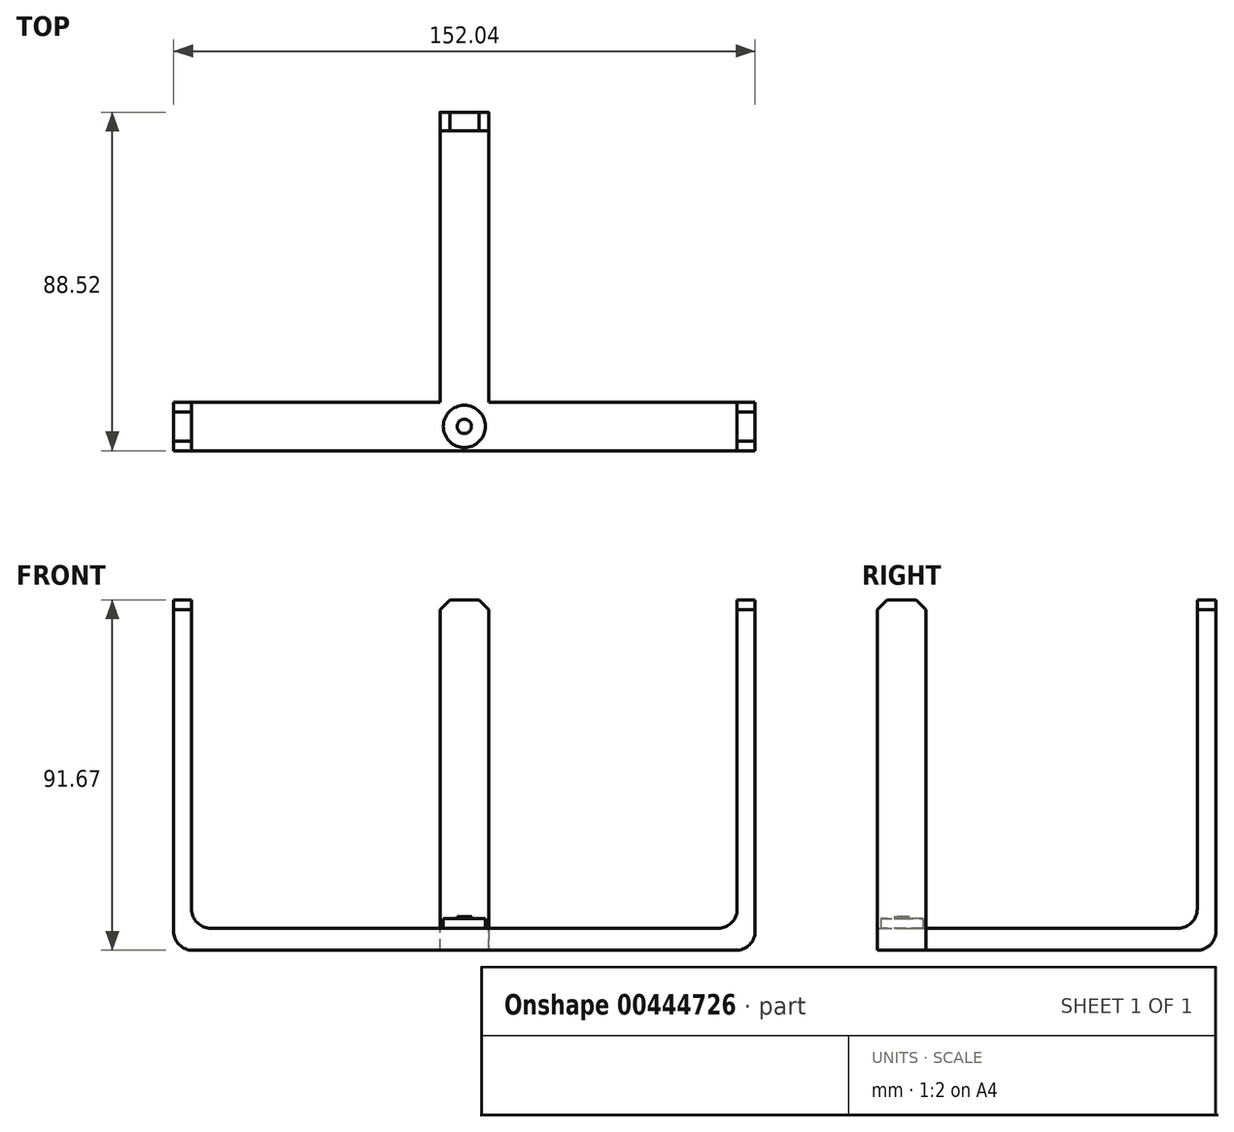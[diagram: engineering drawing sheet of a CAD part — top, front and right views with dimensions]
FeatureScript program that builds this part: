
annotation { "Feature Type Name" : "Feature", "Feature Type Description" : "" }
export const myFeature = defineFeature(function(context is Context, id is Id, definition is map)
    precondition{}
    {
        {
            var Q0;
            Q0=qCreatedBy(makeId("Front.planeOp"),FACE);
            var sketch = newSketch(context, id + "F0", { "sketchPlane" : qUnion([Q0])});
            skLineSegment(sketch, "E0", {"start": v(0, 97.69) * mm, "end": v(0, -49.7) * mm, "construction": true});
            skLineSegment(sketch, "E1", {"start": v(76.02, 85.92) * mm, "end": v(76.02, 0) * mm});
            skLineSegment(sketch, "E2", {"start": v(76.02, 85.92) * mm, "end": v(71.34, 85.92) * mm});
            skLineSegment(sketch, "E3", {"start": v(71.34, 85.92) * mm, "end": v(71.34, 0) * mm});
            skLineSegment(sketch, "E4", {"start": v(71.34, 0) * mm, "end": v(76.02, 0) * mm});
            skLineSegment(sketch, "E5", {"start": v(76.02, -5.75) * mm, "end": v(76.02, 0) * mm});
            skLineSegment(sketch, "E6", {"start": v(76.02, -5.75) * mm, "end": v(0, -5.75) * mm});
            skLineSegment(sketch, "E7.MirrorCS", {"start": v(-71.34, 85.92) * mm, "end": v(-71.34, 0) * mm});
            skLineSegment(sketch, "E8.MirrorCS", {"start": v(-76.02, 85.92) * mm, "end": v(-76.02, 0) * mm});
            skLineSegment(sketch, "E9.MirrorCS", {"start": v(-76.02, 85.92) * mm, "end": v(-71.34, 85.92) * mm});
            skLineSegment(sketch, "E10.MirrorCS", {"start": v(-76.02, -5.75) * mm, "end": v(0, -5.75) * mm});
            skLineSegment(sketch, "E11.MirrorCS", {"start": v(-76.02, -5.75) * mm, "end": v(-76.02, 0) * mm});
            skLineSegment(sketch, "E12.MirrorCS", {"start": v(-71.34, 0) * mm, "end": v(-76.02, 0) * mm});
            skLineSegment(sketch, "E13", {"start": v(-71.34, 0) * mm, "end": v(71.34, 0) * mm});
            skSolve(sketch);
        }
        {
            var Q0;
            Q0=makeQuery(id+"F0.imprint","IMPRINT",FACE,{"disambiguationData":[TD([[makeQuery(id+"F0.imprint","IMPRINT",EDGE,{"derivedFrom":sQuery(id+"F0.wireOp",EDGE,"E4")}),-1.0]])]});
            var Q1;
            Q1=makeQuery(id+"F0.imprint","IMPRINT",FACE,{"disambiguationData":[TD([[makeQuery(id+"F0.imprint","IMPRINT",EDGE,{"derivedFrom":sQuery(id+"F0.wireOp",EDGE,"E7.MirrorCS")}),-1.0]])]});
            var Q2;
            Q2=makeQuery(id+"F0.imprint","IMPRINT",FACE,{"disambiguationData":[TD([[makeQuery(id+"F0.imprint","IMPRINT",EDGE,{"derivedFrom":sQuery(id+"F0.wireOp",EDGE,"E1")}),-1.0]])]});
            extrude(context, id + "F1", {"entities" : qUnion([Q0, Q1, Q2]), "endBound" : BoundingType.SYMMETRIC, "depth" : 12.7 * mm});
        }
        {
            var Q0;
            Q0=qCreatedBy(makeId("Right.planeOp"),FACE);
            var sketch = newSketch(context, id + "F2", { "sketchPlane" : qUnion([Q0])});
            skLineSegment(sketch, "E14", {"start": v(0, 0) * mm, "end": v(77.25, 0) * mm});
            skLineSegment(sketch, "E15", {"start": v(77.25, 0) * mm, "end": v(77.25, -5.75) * mm});
            skLineSegment(sketch, "E16", {"start": v(77.25, -5.75) * mm, "end": v(0, -5.75) * mm});
            skLineSegment(sketch, "E17", {"start": v(77.25, 0) * mm, "end": v(82.15, 0) * mm});
            skLineSegment(sketch, "E18", {"start": v(82.15, 0) * mm, "end": v(82.15, 85.92) * mm});
            skLineSegment(sketch, "E19", {"start": v(82.15, 85.92) * mm, "end": v(77.25, 85.92) * mm});
            skLineSegment(sketch, "E20", {"start": v(77.25, 85.92) * mm, "end": v(77.25, 0) * mm});
            skLineSegment(sketch, "E21", {"start": v(77.25, -5.75) * mm, "end": v(82.4, -5.75) * mm});
            skLineSegment(sketch, "E22", {"start": v(82.4, -5.75) * mm, "end": v(82.15, 0) * mm});
            skLineSegment(sketch, "E23", {"start": v(0, 0) * mm, "end": v(0, -5.75) * mm});
            skLineSegment(sketch, "E24", {"start": v(6.34, 0) * mm, "end": v(6.34, -5.75) * mm});
            skSolve(sketch);
        }
        {
            var Q0;
            Q0=makeQuery(id+"F2.imprint","IMPRINT",FACE,{"disambiguationData":[TD([[makeQuery(id+"F2.imprint","IMPRINT",EDGE,{"derivedFrom":sQuery(id+"F2.wireOp",EDGE,"E17")}),1.0]])]});
            var Q1;
            {var subQ0=sQuery(id+"F2.wireOp",EDGE,"E15");Q1=makeQuery(id+"F2.imprint","IMPRINT",FACE,{"disambiguationData":[TD([[makeQuery(id+"F2.imprint","IMPRINT",EDGE,{"derivedFrom":subQ0}),-1.0]])]});}
            var Q2;
            Q2=makeQuery(id+"F2.imprint","IMPRINT",FACE,{"disambiguationData":[TD([[makeQuery(id+"F2.imprint","IMPRINT",EDGE,{"derivedFrom":sQuery(id+"F2.wireOp",EDGE,"E15")}),1.0]])]});
            extrude(context, id + "F3", {"entities" : qUnion([Q0, Q1, Q2]), "operationType" : NewBodyOperationType.ADD, "endBound" : BoundingType.SYMMETRIC, "depth" : 12.7 * mm});
        }
        {
            var Q0;
            Q0=makeQuery(id+"F3.opExtrude","SWEPT_EDGE",EDGE,{"disambiguationData":[OSD([sQuery(id+"F2.wireOp",EDGE,"E14"),sQuery(id+"F2.wireOp",EDGE,"E15"),sQuery(id+"F2.wireOp",EDGE,"E17"),sQuery(id+"F2.wireOp",EDGE,"E20")])]});
            var Q1;
            Q1=makeQuery(id+"F1.opExtrude","SWEPT_EDGE",EDGE,{"disambiguationData":[OSD([sQuery(id+"F0.wireOp",EDGE,"E7.MirrorCS"),sQuery(id+"F0.wireOp",EDGE,"a127f522-f0cb-4b7a-b9cd-d9324ea2968a0.MirrorCS"),sQuery(id+"F0.wireOp",EDGE,"E12.MirrorCS")])]});
            var Q2;
            Q2=makeQuery(id+"F1.opExtrude","SWEPT_EDGE",EDGE,{"disambiguationData":[OSD([sQuery(id+"F0.wireOp",EDGE,"E3"),sQuery(id+"F0.wireOp",EDGE,"E4"),sQuery(id+"F0.wireOp",EDGE,"ccvVd6eg-Fkt1-mhcF-Id94-4NV2IjYC8jV3")])]});
            var Q3;
            Q3=makeQuery(id+"F1.opExtrude","SWEPT_EDGE",EDGE,{"disambiguationData":[OSD([sQuery(id+"F0.wireOp",EDGE,"E10.MirrorCS"),sQuery(id+"F0.wireOp",EDGE,"E11.MirrorCS")])]});
            var Q4;
            Q4=makeQuery(id+"F1.opExtrude","SWEPT_EDGE",EDGE,{"disambiguationData":[OSD([sQuery(id+"F0.wireOp",EDGE,"E5"),sQuery(id+"F0.wireOp",EDGE,"E6")])]});
            var Q5;
            Q5=makeQuery(id+"F3.opExtrude","SWEPT_EDGE",EDGE,{"disambiguationData":[OSD([sQuery(id+"F2.wireOp",EDGE,"E21"),sQuery(id+"F2.wireOp",EDGE,"E22")])]});
            fillet(context, id + "F4", {"entities" : qUnion([Q0, Q1, Q2, Q3, Q4, Q5]), "radius" : 5.08 * mm, "tangentPropagation" : true, "allowEdgeOverflow" : false});
        }
        {
            var Q0;
            Q0=makeQuery(id+"F1.opExtrude","CAP_EDGE",EDGE,{"disambiguationData":[OSD([sQuery(id+"F0.wireOp",EDGE,"E9.MirrorCS")])],"isStart":false});
            var Q1;
            Q1=makeQuery(id+"F1.opExtrude","CAP_EDGE",EDGE,{"disambiguationData":[OSD([sQuery(id+"F0.wireOp",EDGE,"E9.MirrorCS")])],"isStart":true});
            var Q2;
            Q2=makeQuery(id+"F1.opExtrude","CAP_EDGE",EDGE,{"disambiguationData":[OSD([sQuery(id+"F0.wireOp",EDGE,"E2")])],"isStart":false});
            var Q3;
            Q3=makeQuery(id+"F1.opExtrude","CAP_EDGE",EDGE,{"disambiguationData":[OSD([sQuery(id+"F0.wireOp",EDGE,"E2")])],"isStart":true});
            var Q4;
            Q4=makeQuery(id+"F3.opExtrude","CAP_EDGE",EDGE,{"disambiguationData":[OSD([sQuery(id+"F2.wireOp",EDGE,"E19")])],"isStart":false});
            var Q5;
            Q5=makeQuery(id+"F3.opExtrude","CAP_EDGE",EDGE,{"disambiguationData":[OSD([sQuery(id+"F2.wireOp",EDGE,"E19")])],"isStart":true});
            chamfer(context, id + "F5", {"entities" : qUnion([Q0, Q1, Q2, Q3, Q4, Q5]), "width" : 2.54 * mm, "tangentPropagation" : true});
        }
        {
            var Q0;
            Q0=makeQuery(id+"F3.boolean.opBoolean","MERGE",FACE,{"derivedFrom":[makeQuery(id+"F1.opExtrude","SWEPT_FACE",FACE,{"disambiguationData":[OSD([sQuery(id+"F0.wireOp",EDGE,"E13")])]}),makeQuery(id+"F3.opExtrude","SWEPT_FACE",FACE,{"disambiguationData":[OSD([sQuery(id+"F2.wireOp",EDGE,"E14")])]})]});
            var sketch = newSketch(context, id + "F6", { "sketchPlane" : qUnion([Q0])});
            skCircle(sketch, "E25", {"center": v(0, 0) * mm, "radius": 5.52 * mm});
            skCircle(sketch, "E26", {"center": v(0, 0) * mm, "radius": 1.88 * mm});
            skSolve(sketch);
        }
        {
            var Q0;
            Q0=makeQuery(id+"F6.imprint","IMPRINT",FACE,{"disambiguationData":[TD([[makeQuery(id+"F6.imprint","IMPRINT",EDGE,{"derivedFrom":sQuery(id+"F6.wireOp",EDGE,"E25")}),1.0]])]});
            extrude(context, id + "F7", {"entities" : qUnion([Q0]), "operationType" : NewBodyOperationType.ADD, "depth" : 2.54 * mm});
        }
        {
            var Q0;
            Q0=makeQuery(id+"F7.boolean.opBoolean","SPLIT",FACE,{"disambiguationData":[TD([makeQuery(id+"F7.opExtrude","SWEPT_FACE",FACE,{"disambiguationData":[OSD([sQuery(id+"F6.wireOp",EDGE,"E26")])]})])],"derivedFrom":makeQuery(id+"F3.boolean.opBoolean","MERGE",FACE,{"derivedFrom":[makeQuery(id+"F1.opExtrude","SWEPT_FACE",FACE,{"disambiguationData":[OSD([sQuery(id+"F0.wireOp",EDGE,"E13")])]}),makeQuery(id+"F3.opExtrude","SWEPT_FACE",FACE,{"disambiguationData":[OSD([sQuery(id+"F2.wireOp",EDGE,"E14")])]})]})});
            extrude(context, id + "F8", {"entities" : qUnion([Q0]), "operationType" : NewBodyOperationType.ADD, "depth" : 3.05 * mm});
        }
    });
